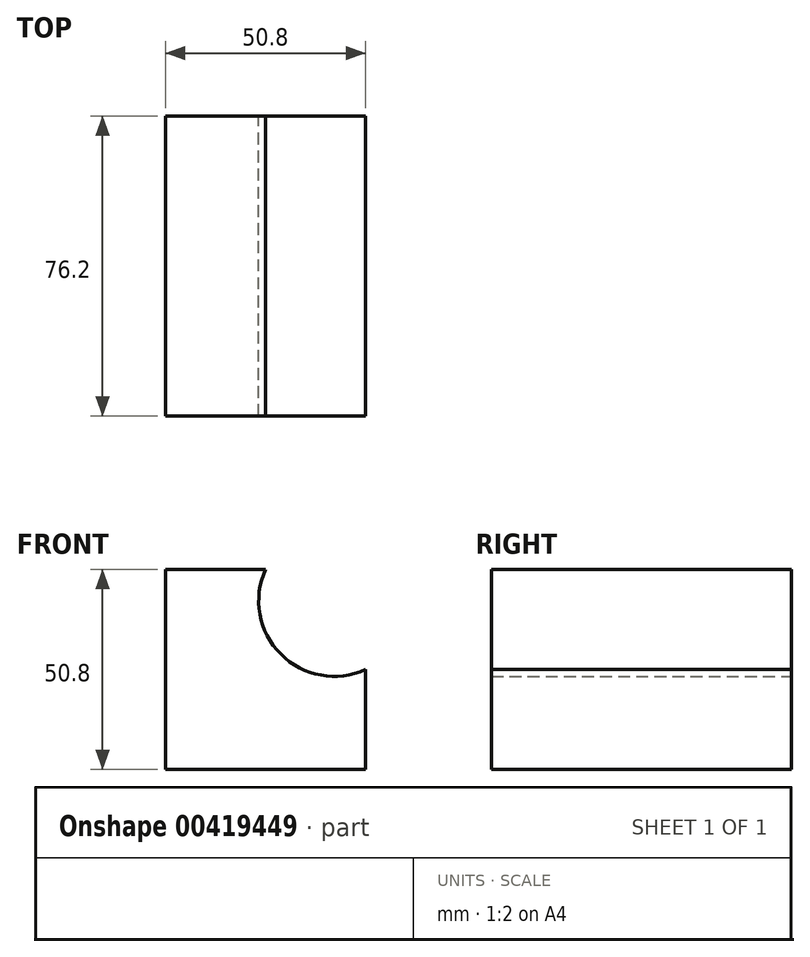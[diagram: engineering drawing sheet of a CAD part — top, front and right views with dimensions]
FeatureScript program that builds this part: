
annotation { "Feature Type Name" : "Feature", "Feature Type Description" : "" }
export const myFeature = defineFeature(function(context is Context, id is Id, definition is map)
    precondition{}
    {
        {
            var Q0;
            Q0=qCreatedBy(makeId("Front.planeOp"),FACE);
            var sketch = newSketch(context, id + "F0", { "sketchPlane" : qUnion([Q0])});
            skLineSegment(sketch, "E0", {"start": v(-50.8, 5.82) * mm, "end": v(-50.8, -44.98) * mm});
            skLineSegment(sketch, "E1", {"start": v(-50.8, -44.98) * mm, "end": v(0, -44.98) * mm});
            skLineSegment(sketch, "E2", {"start": v(0, -44.98) * mm, "end": v(0, -19.58) * mm});
            skLineSegment(sketch, "E3", {"start": v(-50.8, 5.82) * mm, "end": v(-25.4, 5.82) * mm});
            skArc(sketch, "E4", {"start": v(-25.4, 5.82) * mm, "mid": v(-21.51, -15.7) * mm, "end": v(0, -19.58) * mm});
            skSolve(sketch);
        }
        {
            var Q0;
            Q0=makeQuery(id+"F0.imprint","IMPRINT",FACE,{"disambiguationData":[TD([[makeQuery(id+"F0.imprint","IMPRINT",EDGE,{"derivedFrom":sQuery(id+"F0.wireOp",EDGE,"E0")}),1.0]])]});
            extrude(context, id + "F1", {"entities" : qUnion([Q0]), "depth" : 76.2 * mm});
        }
    });
